# Revit family: Haworth_Tibas_Desk_MeetingTable_EU_PRELIMINARY1
name_source: partatom
category: Furniture
units: mm (PartAtom-declared; Revit-internal decimal feet)

## family parameters
Always vertical = Yes
Cut with Voids When Loaded = No
OmniClass Number = 23.40.70.14.64.11
OmniClass Title = Office Furniture
Room Calculation Point = No
Shared = No
Work Plane-Based = No

## types (5) — shared parameters
Assembly Code = E2020200
Description = Haworth - Tibas - Desk - Meeting Table
Flip Top Finish = Haworth _ Paint _ Metallic Silver
Manufacturer = Haworth
Model = TIMPXXXXXL
Product URL = https://www.haworth.com
Revision Number = 1
Size = Verify Final Dim.w/ Haworth
Trim Finish = Haworth _ Polymer _ Undecided
URL = https://www.haworth.com
Warranty = http://www.haworth.com
Worksurface Size = 140 x 140, 220 x 110, 240 x 100, 120dia

## per-type parameters (varying)
| type | Actual Depth | Actual Height | Actual Width | Beam Width | Boat Shape | Leg Depth | Leg Height | Leg Width | Rectangle | Rectangular Table EL | Rectangular Table Large | Rectangular Table OL | Round Table |
| 140 x 140 OL | 140 cm | 75 cm | 140 cm | 134 cm | No | 130 cm | 72 cm | 6 cm | Yes | No | No | Yes | No |
| 140 X 140 EL | 140 cm | 84 cm | 140 cm | 105 cm | No | 100 cm | 80 cm | 25 cm | Yes | Yes | No | No | No |
| 120dia | 120 cm | 84 cm | 120 cm | 90 cm | No | 70 cm | 80 cm | 20 cm | No | No | No | No | Yes |
| 240 x 100 | 100 cm | 84 cm | 240 cm | 175 cm | No | 80 cm | 80 cm | 35 cm | Yes | No | Yes | No | No |
| 220 x 110 | 110 cm | 84 cm | 220 cm | 170 cm | Yes | 80 cm | 80 cm | 30 cm | No | No | No | No | No |

## geometry (parser evidence)
native form markers: Sweep x36
no freeform markers — native parametric forms only
